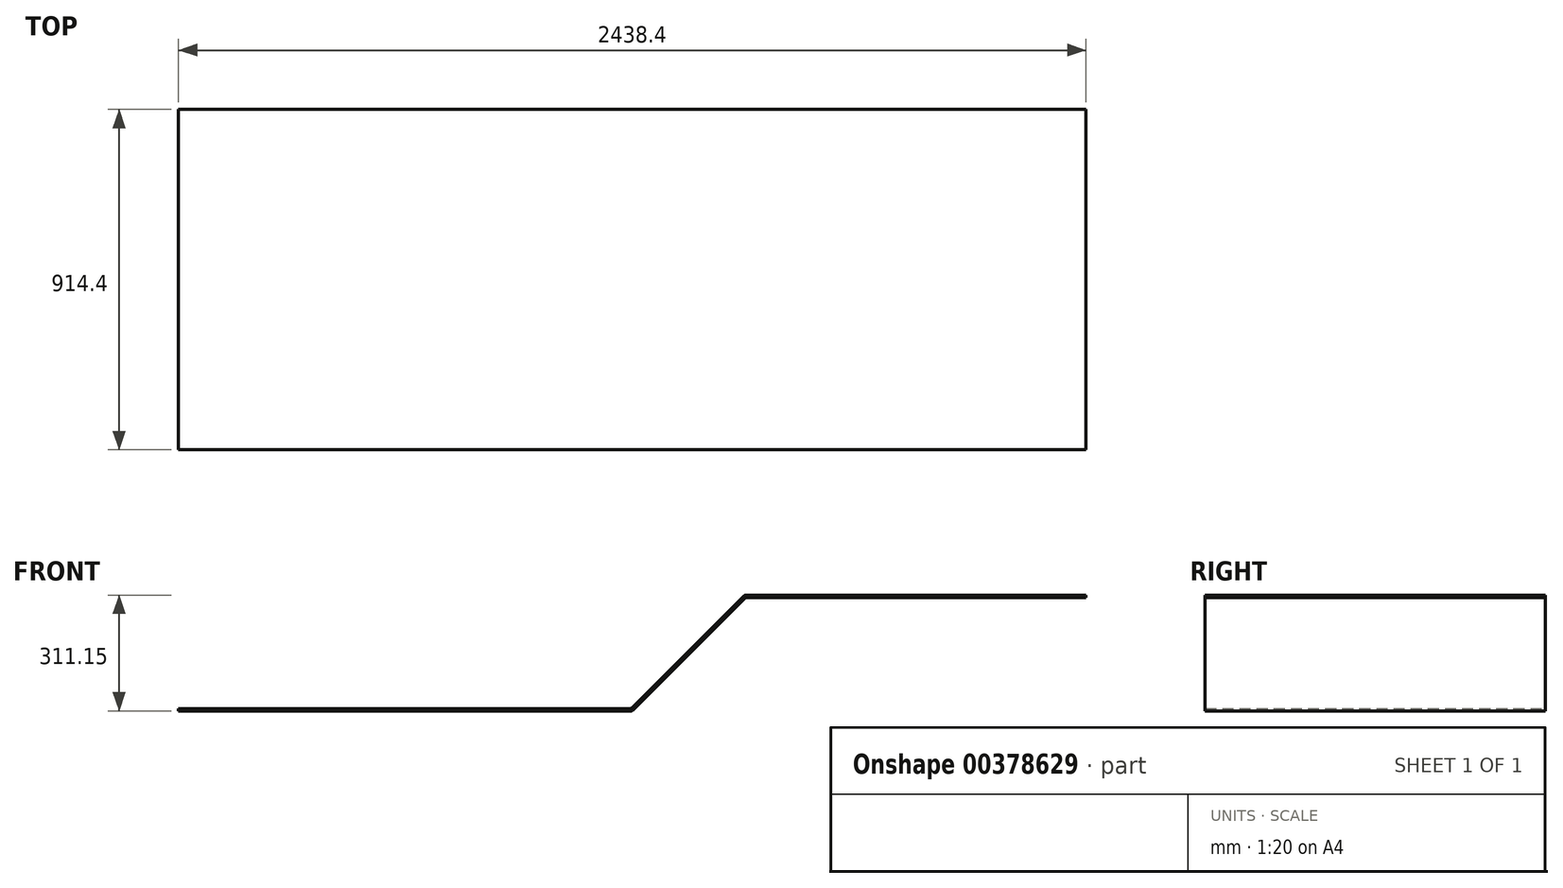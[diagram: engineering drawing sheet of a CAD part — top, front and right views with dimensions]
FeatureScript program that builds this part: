
annotation { "Feature Type Name" : "Feature", "Feature Type Description" : "" }
export const myFeature = defineFeature(function(context is Context, id is Id, definition is map)
    precondition{}
    {
        {
            var Q0;
            Q0=qCreatedBy(makeId("Front.planeOp"),FACE);
            var sketch = newSketch(context, id + "F0", { "sketchPlane" : qUnion([Q0])});
            skLineSegment(sketch, "E0", {"start": v(-2.63, 0) * mm, "end": v(-1219.2, 0) * mm});
            skLineSegment(sketch, "E1", {"start": v(1.86, 1.86) * mm, "end": v(302.94, 302.94) * mm});
            skLineSegment(sketch, "E2", {"start": v(307.43, 304.8) * mm, "end": v(1219.2, 304.8) * mm});
            skLineSegment(sketch, "E3.0", {"start": v(-5.26, 6.35) * mm, "end": v(-1219.2, 6.35) * mm});
            skLineSegment(sketch, "E3.1", {"start": v(-0.77, 8.2) * mm, "end": v(300.3, 309.3) * mm});
            skLineSegment(sketch, "E3.2", {"start": v(304.8, 311.15) * mm, "end": v(1219.2, 311.15) * mm});
            skLineSegment(sketch, "E4", {"start": v(1219.2, 311.15) * mm, "end": v(1219.2, 304.8) * mm});
            skLineSegment(sketch, "E5", {"start": v(-1219.2, 6.35) * mm, "end": v(-1219.2, 0) * mm});
            skPoint(sketch, "E6.visualSharp", {"position": v(0, 0) * mm});
            skArc(sketch, "E6.filletArc", {"start": v(-2.63, 0) * mm, "mid": v(-0.2, 0.48) * mm, "end": v(1.86, 1.86) * mm});
            skPoint(sketch, "E7.visualSharp", {"position": v(304.8, 304.8) * mm});
            skArc(sketch, "E7.filletArc", {"start": v(307.43, 304.8) * mm, "mid": v(305, 304.32) * mm, "end": v(302.94, 302.94) * mm});
            skPoint(sketch, "E8.visualSharp", {"position": v(302.17, 311.15) * mm});
            skArc(sketch, "E8.filletArc", {"start": v(304.8, 311.15) * mm, "mid": v(302.37, 310.67) * mm, "end": v(300.3, 309.3) * mm});
            skArc(sketch, "E9.filletArc", {"start": v(-5.26, 6.35) * mm, "mid": v(-2.83, 6.83) * mm, "end": v(-0.77, 8.2) * mm});
            skSolve(sketch);
        }
        {
            var Q0;
            Q0 = qSketchRegion(id + "F0", true);
            extrude(context, id + "F1", {"entities" : qUnion([Q0]), "endBound" : BoundingType.SYMMETRIC, "depth" : 914.4 * mm});
        }
    });
